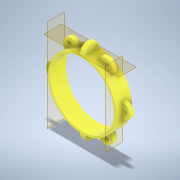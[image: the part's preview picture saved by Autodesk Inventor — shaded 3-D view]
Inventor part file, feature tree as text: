
AUTODESK INVENTOR PART (.ipt)
format: ipt  version: 2021.2 (Build 252289000, 289)  size: 234,496 bytes
history: native  units: in
note: dims shown in document units (in); Inventor stores cm internally (conversion verified against a paired STEP export)
features: extrude x6, sketch x6, plane x3, fillet x2, pattern_circular x2
ambient origin geometry x8: Origin, YZ Plane, XZ Plane, XY Plane, X Axis, Y Axis, Z Axis, Center Point
bodies: Solid1 (feature_tree)
feature tree (19):
  extrude  "Extrusion1"  Depth=4.25in
  plane  "Work Plane1"
  plane  "Work Plane2"
  extrude  "Extrusion3"  Depth=2.125in
  fillet  "Fillet1"  Radius=2.125in
  extrude  "Extrusion4"  TaperAngle=0.0deg  [1 undecoded]
  pattern_circular  "Circular Pattern2"  [2 undecoded]
  plane  "Work Plane3"
  extrude  "Extrusion5"  Depth=0.5in TaperAngle=0.0deg
  extrude  "Extrusion6"  Depth=0.25in TaperAngle=360.0deg
  fillet  "Fillet2"  [1 undecoded]
  extrude  "Extrusion7"  Depth=1.0in
  pattern_circular  "Circular Pattern3"  [2 undecoded]
  sketch  "Sketch1"  dims[d0=4.0in d1=4.25in]
  sketch  "Sketch3"  dims[d2=1.0in d3=0.0in d4=1.5in d10=2.125in]
  sketch  "Sketch4"  dims[d11=0.25in d12=0.0in]
  sketch  "Sketch5"  dims[d13=0.5in d14=0.0in]
  sketch  "Sketch6"  dims[d15=0.5in]
  sketch  "Sketch7"  dims[d16=0.125in d17=0.2in d18=0.5in d19=0.0in d20=0.7874in d21=360.0deg d23=-2.125in d24=1.0in d25=0.25in d26=0.5in d27=0.0in d28=0.1in d29=0.0in d30=0.5in d31=0.0in d32=0.5in d33=0.25in d34=0.2in d35=0.5in d36=0.0in d37=2.3622in d38=360.0deg d40=0.25in d41=0.125in d42=0.25in d43=0.2in]
note: 6 required parameter values undecoded (feature->parameter linkage not recoverable at this tier; creation-order binding heuristic only, values carry confidence <= 0.55)
